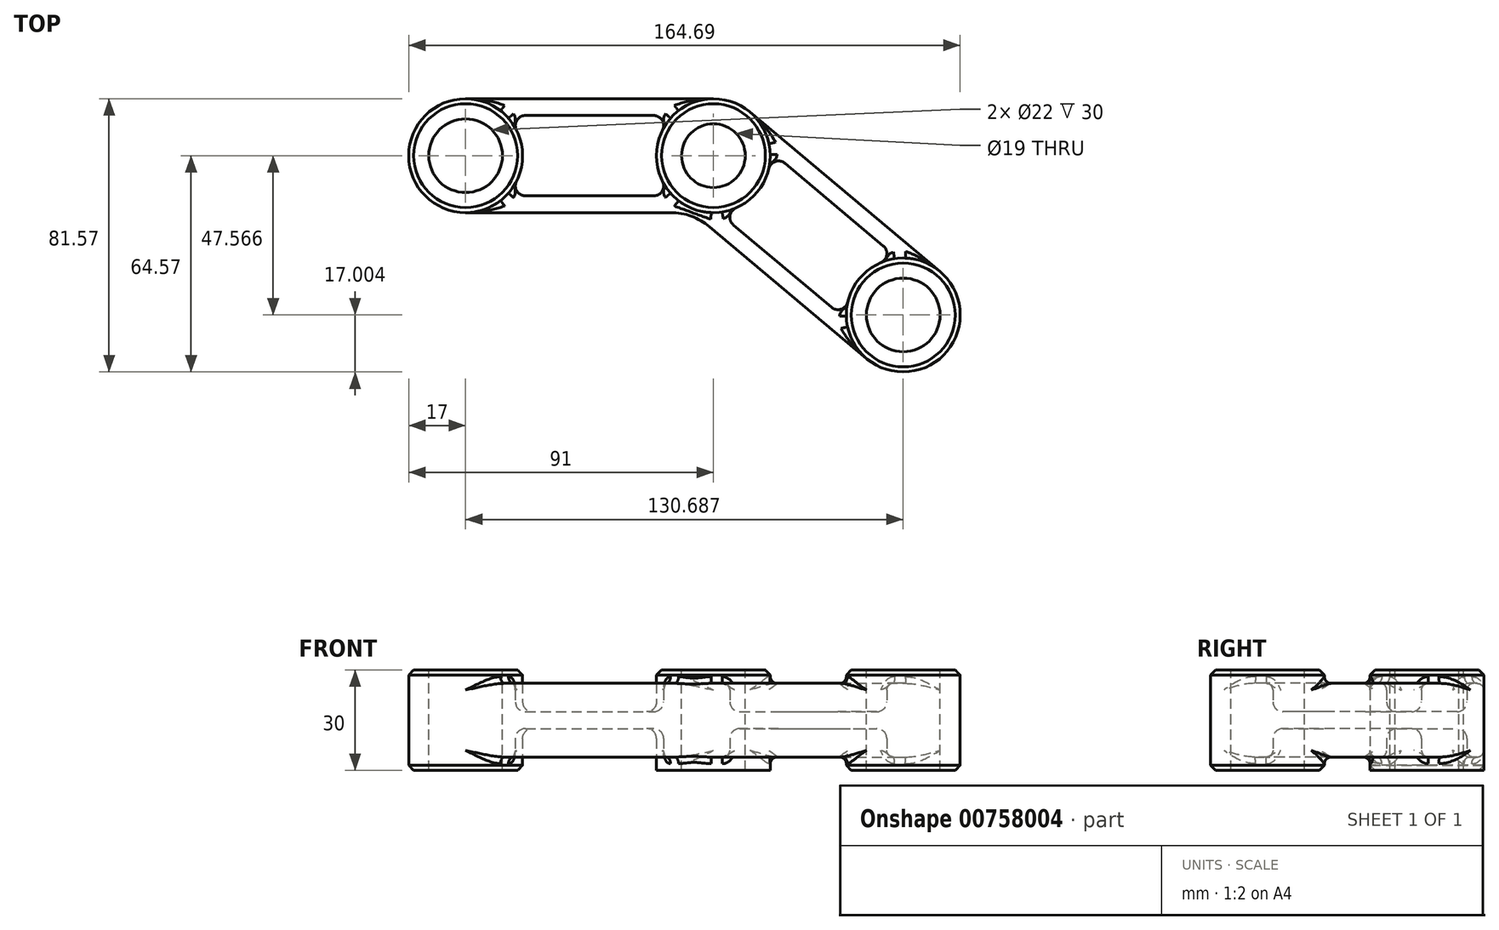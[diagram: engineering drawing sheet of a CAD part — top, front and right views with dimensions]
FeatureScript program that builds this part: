
annotation { "Feature Type Name" : "Feature", "Feature Type Description" : "" }
export const myFeature = defineFeature(function(context is Context, id is Id, definition is map)
    precondition{}
    {
        {
            var Q0;
            Q0=qCreatedBy(makeId("Top.planeOp"),FACE);
            var sketch = newSketch(context, id + "F0", { "sketchPlane" : qUnion([Q0])});
            skLineSegment(sketch, "E0", {"start": v(0, 0) * mm, "end": v(74, 0) * mm, "construction": true});
            skLineSegment(sketch, "E1", {"start": v(74, 0) * mm, "end": v(130.69, -47.57) * mm, "construction": true});
            skCircle(sketch, "E2", {"center": v(0, 0) * mm, "radius": 17 * mm});
            skCircle(sketch, "E3", {"center": v(74, 0) * mm, "radius": 17 * mm});
            skCircle(sketch, "E4", {"center": v(130.69, -47.57) * mm, "radius": 17 * mm});
            skCircle(sketch, "E5", {"center": v(0, 0) * mm, "radius": 11 * mm});
            skCircle(sketch, "E6", {"center": v(130.69, -47.57) * mm, "radius": 11 * mm});
            skCircle(sketch, "E7", {"center": v(74, 0) * mm, "radius": 9.5 * mm});
            skLineSegment(sketch, "E8", {"start": v(0, 0) * mm, "end": v(74, 0) * mm});
            skLineSegment(sketch, "E9", {"start": v(74, 0) * mm, "end": v(130.69, -47.57) * mm});
            skSolve(sketch);
        }
        {
            var Q0;
            Q0=qCreatedBy(makeId("Right.planeOp"),FACE);
            var sketch = newSketch(context, id + "F1", { "sketchPlane" : qUnion([Q0])});
            skLineSegment(sketch, "E10", {"start": v(-22.72, 0) * mm, "end": v(23.89, 0) * mm, "construction": true});
            skLineSegment(sketch, "E11", {"start": v(17, 0) * mm, "end": v(17, -11) * mm});
            skLineSegment(sketch, "E12", {"start": v(17, -11) * mm, "end": v(12, -11) * mm});
            skLineSegment(sketch, "E13", {"start": v(12, -11) * mm, "end": v(12, -2.5) * mm});
            skLineSegment(sketch, "E14", {"start": v(12, -2.5) * mm, "end": v(-12, -2.5) * mm});
            skLineSegment(sketch, "E15", {"start": v(-12, -2.5) * mm, "end": v(-12, -11) * mm});
            skLineSegment(sketch, "E16", {"start": v(-12, -11) * mm, "end": v(-17, -11) * mm});
            skLineSegment(sketch, "E17", {"start": v(-17, -11) * mm, "end": v(-17, 0) * mm});
            skLineSegment(sketch, "E18.MirrorCS", {"start": v(12, 2.5) * mm, "end": v(-12, 2.5) * mm});
            skLineSegment(sketch, "E19.MirrorCS", {"start": v(12, 11) * mm, "end": v(12, 2.5) * mm});
            skLineSegment(sketch, "E20.MirrorCS", {"start": v(-12, 2.5) * mm, "end": v(-12, 11) * mm});
            skLineSegment(sketch, "E21.MirrorCS", {"start": v(17, 0) * mm, "end": v(17, 11) * mm});
            skLineSegment(sketch, "E22.MirrorCS", {"start": v(-17, 11) * mm, "end": v(-17, 0) * mm});
            skLineSegment(sketch, "E23.MirrorCS", {"start": v(-12, 11) * mm, "end": v(-17, 11) * mm});
            skLineSegment(sketch, "E24.MirrorCS", {"start": v(17, 11) * mm, "end": v(12, 11) * mm});
            skLineSegment(sketch, "E25", {"start": v(0, 0) * mm, "end": v(0, 16.88) * mm, "construction": true});
            skSolve(sketch);
        }
        {
            var Q0;
            Q0=makeQuery(id+"F1.imprint","IMPRINT",FACE,{"disambiguationData":[TD([[makeQuery(id+"F1.imprint","IMPRINT",EDGE,{"derivedFrom":sQuery(id+"F1.wireOp",EDGE,"E11")}),-1.0]])]});
            var Q1;
            Q1=sQuery(id+"F0.wireOp",EDGE,"E8");
            var Q2;
            Q2=sQuery(id+"F0.wireOp",EDGE,"E9");
            sweep(context, id + "F2", {"profiles" : qUnion([Q0]), "path" : qUnion([Q1, Q2])});
        }
        {
            var Q0;
            Q0=makeQuery(id+"F0.imprint","IMPRINT",FACE,{"disambiguationData":[TD([[makeQuery(id+"F0.imprint","IMPRINT",EDGE,{"derivedFrom":sQuery(id+"F0.wireOp",EDGE,"E5")}),1.0]])]});
            var Q1;
            Q1=makeQuery(id+"F0.imprint","IMPRINT",FACE,{"disambiguationData":[TD([[makeQuery(id+"F0.imprint","IMPRINT",EDGE,{"derivedFrom":sQuery(id+"F0.wireOp",EDGE,"E2")}),1.0]])]});
            var Q2;
            {var subQ0=sQuery(id+"F0.wireOp",EDGE,"E8");var subQ1=sQuery(id+"F0.wireOp",EDGE,"E7");var subQ2=makeQuery(id+"F0.imprint","INTERSECT",VERTEX,{"derivedFrom":[subQ1,subQ0]});Q2=makeQuery(id+"F0.imprint","IMPRINT",FACE,{"disambiguationData":[TD([[makeQuery(id+"F0.imprint","IMPRINT",EDGE,{"disambiguationData":[TD([[subQ2,-1.0]])],"derivedFrom":subQ1}),1.0]])]});}
            var Q3;
            {var subQ0=sQuery(id+"F0.wireOp",EDGE,"E8");var subQ1=sQuery(id+"F0.wireOp",EDGE,"E7");var subQ2=makeQuery(id+"F0.imprint","INTERSECT",VERTEX,{"derivedFrom":[subQ1,subQ0]});Q3=makeQuery(id+"F0.imprint","IMPRINT",FACE,{"disambiguationData":[TD([[makeQuery(id+"F0.imprint","IMPRINT",EDGE,{"disambiguationData":[TD([[subQ2,1.0]])],"derivedFrom":subQ1}),1.0]])]});}
            var Q4;
            {var subQ0=sQuery(id+"F0.wireOp",EDGE,"E8");var subQ1=sQuery(id+"F0.wireOp",EDGE,"E3");var subQ2=makeQuery(id+"F0.imprint","INTERSECT",VERTEX,{"derivedFrom":[subQ1,subQ0]});Q4=makeQuery(id+"F0.imprint","IMPRINT",FACE,{"disambiguationData":[TD([[makeQuery(id+"F0.imprint","IMPRINT",EDGE,{"disambiguationData":[TD([[subQ2,1.0]])],"derivedFrom":subQ1}),1.0]])]});}
            var Q5;
            {var subQ0=sQuery(id+"F0.wireOp",EDGE,"E8");var subQ1=sQuery(id+"F0.wireOp",EDGE,"E3");var subQ2=makeQuery(id+"F0.imprint","INTERSECT",VERTEX,{"derivedFrom":[subQ1,subQ0]});Q5=makeQuery(id+"F0.imprint","IMPRINT",FACE,{"disambiguationData":[TD([[makeQuery(id+"F0.imprint","IMPRINT",EDGE,{"disambiguationData":[TD([[subQ2,-1.0]])],"derivedFrom":subQ1}),1.0]])]});}
            var Q6;
            Q6=makeQuery(id+"F0.imprint","IMPRINT",FACE,{"disambiguationData":[TD([[makeQuery(id+"F0.imprint","IMPRINT",EDGE,{"derivedFrom":sQuery(id+"F0.wireOp",EDGE,"E4")}),1.0]])]});
            var Q7;
            Q7=makeQuery(id+"F0.imprint","IMPRINT",FACE,{"disambiguationData":[TD([[makeQuery(id+"F0.imprint","IMPRINT",EDGE,{"derivedFrom":sQuery(id+"F0.wireOp",EDGE,"E6")}),1.0]])]});
            extrude(context, id + "F3", {"entities" : qUnion([Q0, Q1, Q2, Q3, Q4, Q5, Q6, Q7]), "operationType" : NewBodyOperationType.ADD, "depth" : 30 * mm, "offsetDistance" : 25 * mm, "symmetric" : true});
        }
        {
            var Q0;
            Q0=makeQuery(id+"F0.imprint","IMPRINT",FACE,{"disambiguationData":[TD([[makeQuery(id+"F0.imprint","IMPRINT",EDGE,{"derivedFrom":sQuery(id+"F0.wireOp",EDGE,"E5")}),1.0]])]});
            var Q1;
            {var subQ0=sQuery(id+"F0.wireOp",EDGE,"E8");var subQ1=sQuery(id+"F0.wireOp",EDGE,"E7");var subQ2=makeQuery(id+"F0.imprint","INTERSECT",VERTEX,{"derivedFrom":[subQ1,subQ0]});Q1=makeQuery(id+"F0.imprint","IMPRINT",FACE,{"disambiguationData":[TD([[makeQuery(id+"F0.imprint","IMPRINT",EDGE,{"disambiguationData":[TD([[subQ2,1.0]])],"derivedFrom":subQ1}),1.0]])]});}
            var Q2;
            {var subQ0=sQuery(id+"F0.wireOp",EDGE,"E8");var subQ1=sQuery(id+"F0.wireOp",EDGE,"E7");var subQ2=makeQuery(id+"F0.imprint","INTERSECT",VERTEX,{"derivedFrom":[subQ1,subQ0]});Q2=makeQuery(id+"F0.imprint","IMPRINT",FACE,{"disambiguationData":[TD([[makeQuery(id+"F0.imprint","IMPRINT",EDGE,{"disambiguationData":[TD([[subQ2,-1.0]])],"derivedFrom":subQ1}),1.0]])]});}
            var Q3;
            Q3=makeQuery(id+"F0.imprint","IMPRINT",FACE,{"disambiguationData":[TD([[makeQuery(id+"F0.imprint","IMPRINT",EDGE,{"derivedFrom":sQuery(id+"F0.wireOp",EDGE,"E6")}),1.0]])]});
            extrude(context, id + "F4", {"entities" : qUnion([Q0, Q1, Q2, Q3]), "operationType" : NewBodyOperationType.REMOVE, "oppositeDirection" : true, "depth" : 30 * mm, "offsetDistance" : 25 * mm, "symmetric" : true});
        }
        {
            var Q0;
            {var subQ0=sQuery(id+"F1.wireOp",EDGE,"E21.MirrorCS");var subQ1=sQuery(id+"F1.wireOp",EDGE,"E11");var subQ2=sQuery(id+"F0.wireOp",EDGE,"E8");var subQ3=makeQuery(id+"F2.opSweep","SWEPT_FACE",FACE,{"disambiguationData":[OSD([subQ2,sQuery(id+"F1.wireOp",EDGE,"E24.MirrorCS")])]});Q0=makeQuery(id+"F3.boolean.opBoolean","SPLIT",FACE,{"disambiguationData":[TD([makeQuery(id+"F2.opSweep","SWEPT_FACE",FACE,{"disambiguationData":[OSD([subQ2,subQ1,subQ0])]}),subQ3,makeQuery(id+"F2.opSweep","SWEPT_FACE",FACE,{"disambiguationData":[OSD([sQuery(id+"F0.wireOp",EDGE,"E9"),subQ1,subQ0])]}),makeQuery(id+"F3.opExtrude","SWEPT_FACE",FACE,{"disambiguationData":[OSD([sQuery(id+"F0.wireOp",EDGE,"E3")])]})])],"derivedFrom":subQ3});}
            var sketch = newSketch(context, id + "F5", { "sketchPlane" : qUnion([Q0])});
            skLineSegment(sketch, "E26.0.0", {"start": v(80.19, 17) * mm, "end": v(74, 17) * mm});
            skArc(sketch, "E26.0.1", {"start": v(74, 17) * mm, "mid": v(79.81, 15.97) * mm, "end": v(84.93, 13.02) * mm});
            skLineSegment(sketch, "E26.0.2", {"start": v(84.93, 13.02) * mm, "end": v(80.19, 17) * mm});
            skSolve(sketch);
        }
        {
            var Q0;
            Q0=qSketchRegion(id+"F5",true);
            extrude(context, id + "F6", {"entities" : qUnion([Q0]), "operationType" : NewBodyOperationType.REMOVE, "endBound" : BoundingType.THROUGH_ALL, "oppositeDirection" : true, "depth" : 25 * mm, "offsetDistance" : 25 * mm});
        }
        {
            var Q0;
            Q0=makeQuery(id+"F2.opSweep","MID_CAP_EDGE",EDGE,{"disambiguationData":[OSD([sQuery(id+"F0.wireOp",VERTEX,"E9.start"),sQuery(id+"F1.wireOp",EDGE,"E17"),sQuery(id+"F1.wireOp",EDGE,"E22.MirrorCS")])],"capPos":1.0});
            fillet(context, id + "F7", {"entities" : qUnion([Q0]), "radius" : 18 * mm, "tangentPropagation" : true, "allowEdgeOverflow" : false});
        }
        {
            var Q0;
            Q0=makeQuery(id+"F3.opExtrude","CAP_EDGE",EDGE,{"disambiguationData":[OSD([sQuery(id+"F0.wireOp",EDGE,"E2")])],"isStart":false});
            var Q1;
            Q1=makeQuery(id+"F3.opExtrude","CAP_EDGE",EDGE,{"disambiguationData":[OSD([sQuery(id+"F0.wireOp",EDGE,"E2")])],"isStart":true});
            var Q2;
            Q2=makeQuery(id+"F3.opExtrude","CAP_EDGE",EDGE,{"disambiguationData":[OSD([sQuery(id+"F0.wireOp",EDGE,"E3")])],"isStart":true});
            var Q3;
            Q3=makeQuery(id+"F3.opExtrude","CAP_EDGE",EDGE,{"disambiguationData":[OSD([sQuery(id+"F0.wireOp",EDGE,"E3")])],"isStart":false});
            var Q4;
            Q4=makeQuery(id+"F3.opExtrude","CAP_EDGE",EDGE,{"disambiguationData":[OSD([sQuery(id+"F0.wireOp",EDGE,"E4")])],"isStart":false});
            var Q5;
            Q5=makeQuery(id+"F3.opExtrude","CAP_EDGE",EDGE,{"disambiguationData":[OSD([sQuery(id+"F0.wireOp",EDGE,"E4")])],"isStart":true});
            chamfer(context, id + "F8", {"entities" : qUnion([Q0, Q1, Q2, Q3, Q4, Q5]), "width" : 1.5 * mm, "tangentPropagation" : true});
        }
        {
            var Q0;
            Q0=makeQuery(id+"F2.opSweep","SWEPT_EDGE",EDGE,{"disambiguationData":[OSD([sQuery(id+"F0.wireOp",EDGE,"E8"),sQuery(id+"F1.wireOp",EDGE,"E22.MirrorCS"),sQuery(id+"F1.wireOp",EDGE,"E23.MirrorCS")])]});
            var Q1;
            Q1=makeQuery(id+"F2.opSweep","SWEPT_EDGE",EDGE,{"disambiguationData":[OSD([sQuery(id+"F0.wireOp",EDGE,"E8"),sQuery(id+"F1.wireOp",EDGE,"E16"),sQuery(id+"F1.wireOp",EDGE,"E17")])]});
            var Q2;
            {var subQ0=sQuery(id+"F1.wireOp",EDGE,"E21.MirrorCS");var subQ1=sQuery(id+"F0.wireOp",EDGE,"E8");var subQ2=sQuery(id+"F1.wireOp",EDGE,"E24.MirrorCS");Q2=makeQuery(id+"F3.boolean.opBoolean","SPLIT",EDGE,{"disambiguationData":[TD([makeQuery(id+"F3.opExtrude","SWEPT_FACE",FACE,{"disambiguationData":[OSD([sQuery(id+"F0.wireOp",EDGE,"E2")])]})])],"derivedFrom":makeQuery(id+"F2.opSweep","SWEPT_EDGE",EDGE,{"disambiguationData":[OSD([subQ1,subQ0,subQ2])]})});}
            var Q3;
            {var subQ0=sQuery(id+"F1.wireOp",EDGE,"E24.MirrorCS");var subQ1=sQuery(id+"F1.wireOp",EDGE,"E21.MirrorCS");var subQ2=sQuery(id+"F0.wireOp",EDGE,"E9");Q3=makeQuery(id+"F3.boolean.opBoolean","SPLIT",EDGE,{"disambiguationData":[TD([makeQuery(id+"F3.opExtrude","SWEPT_FACE",FACE,{"disambiguationData":[OSD([sQuery(id+"F0.wireOp",EDGE,"E4")])]})])],"derivedFrom":makeQuery(id+"F2.opSweep","SWEPT_EDGE",EDGE,{"disambiguationData":[OSD([subQ2,subQ1,subQ0])]})});}
            var Q4;
            {var subQ0=sQuery(id+"F1.wireOp",EDGE,"E11");var subQ1=sQuery(id+"F0.wireOp",EDGE,"E8");var subQ2=sQuery(id+"F1.wireOp",EDGE,"E12");Q4=makeQuery(id+"F3.boolean.opBoolean","SPLIT",EDGE,{"disambiguationData":[TD([makeQuery(id+"F3.opExtrude","SWEPT_FACE",FACE,{"disambiguationData":[OSD([sQuery(id+"F0.wireOp",EDGE,"E2")])]})])],"derivedFrom":makeQuery(id+"F2.opSweep","SWEPT_EDGE",EDGE,{"disambiguationData":[OSD([subQ1,subQ0,subQ2])]})});}
            var Q5;
            {var subQ0=sQuery(id+"F1.wireOp",EDGE,"E12");var subQ1=sQuery(id+"F1.wireOp",EDGE,"E11");var subQ2=sQuery(id+"F0.wireOp",EDGE,"E9");Q5=makeQuery(id+"F3.boolean.opBoolean","SPLIT",EDGE,{"disambiguationData":[TD([makeQuery(id+"F3.opExtrude","SWEPT_FACE",FACE,{"disambiguationData":[OSD([sQuery(id+"F0.wireOp",EDGE,"E4")])]})])],"derivedFrom":makeQuery(id+"F2.opSweep","SWEPT_EDGE",EDGE,{"disambiguationData":[OSD([subQ2,subQ1,subQ0])]})});}
            fillet(context, id + "F9", {"entities" : qUnion([Q0, Q1, Q2, Q3, Q4, Q5]), "radius" : 2 * mm, "tangentPropagation" : true, "allowEdgeOverflow" : false});
        }
        {
            var Q0;
            {var subQ0=sQuery(id+"F0.wireOp",EDGE,"E8");Q0=makeQuery(id+"F3.boolean.opBoolean","SPLIT",FACE,{"disambiguationData":[TD([makeQuery(id+"F3.opExtrude","SWEPT_FACE",FACE,{"disambiguationData":[OSD([sQuery(id+"F0.wireOp",EDGE,"E2")])]})])],"derivedFrom":makeQuery(id+"F2.opSweep","SWEPT_FACE",FACE,{"disambiguationData":[OSD([subQ0,sQuery(id+"F1.wireOp",EDGE,"E18.MirrorCS")])]})});}
            var Q1;
            Q1=makeQuery(id+"F3.boolean.opBoolean","INTERSECT",EDGE,{"derivedFrom":[makeQuery(id+"F2.opSweep","SWEPT_FACE",FACE,{"disambiguationData":[OSD([sQuery(id+"F0.wireOp",EDGE,"E8"),sQuery(id+"F1.wireOp",EDGE,"E19.MirrorCS")])]}),makeQuery(id+"F3.opExtrude","SWEPT_FACE",FACE,{"disambiguationData":[OSD([sQuery(id+"F0.wireOp",EDGE,"E3")])]})]});
            var Q2;
            Q2=makeQuery(id+"F3.boolean.opBoolean","INTERSECT",EDGE,{"derivedFrom":[makeQuery(id+"F2.opSweep","SWEPT_FACE",FACE,{"disambiguationData":[OSD([sQuery(id+"F0.wireOp",EDGE,"E8"),sQuery(id+"F1.wireOp",EDGE,"E19.MirrorCS")])]}),makeQuery(id+"F3.opExtrude","SWEPT_FACE",FACE,{"disambiguationData":[OSD([sQuery(id+"F0.wireOp",EDGE,"E2")])]})]});
            var Q3;
            Q3=makeQuery(id+"F3.boolean.opBoolean","INTERSECT",EDGE,{"derivedFrom":[makeQuery(id+"F2.opSweep","SWEPT_FACE",FACE,{"disambiguationData":[OSD([sQuery(id+"F0.wireOp",EDGE,"E8"),sQuery(id+"F1.wireOp",EDGE,"E20.MirrorCS")])]}),makeQuery(id+"F3.opExtrude","SWEPT_FACE",FACE,{"disambiguationData":[OSD([sQuery(id+"F0.wireOp",EDGE,"E2")])]})]});
            var Q4;
            Q4=makeQuery(id+"F3.boolean.opBoolean","INTERSECT",EDGE,{"derivedFrom":[makeQuery(id+"F2.opSweep","SWEPT_FACE",FACE,{"disambiguationData":[OSD([sQuery(id+"F0.wireOp",EDGE,"E8"),sQuery(id+"F1.wireOp",EDGE,"E20.MirrorCS")])]}),makeQuery(id+"F3.opExtrude","SWEPT_FACE",FACE,{"disambiguationData":[OSD([sQuery(id+"F0.wireOp",EDGE,"E3")])]})]});
            var Q5;
            Q5=makeQuery(id+"F3.boolean.opBoolean","SPLIT",FACE,{"disambiguationData":[TD([makeQuery(id+"F3.opExtrude","SWEPT_FACE",FACE,{"disambiguationData":[OSD([sQuery(id+"F0.wireOp",EDGE,"E4")])]})])],"derivedFrom":makeQuery(id+"F2.opSweep","SWEPT_FACE",FACE,{"disambiguationData":[OSD([sQuery(id+"F0.wireOp",EDGE,"E8"),sQuery(id+"F1.wireOp",EDGE,"E18.MirrorCS")])]})});
            var Q6;
            Q6=makeQuery(id+"F3.boolean.opBoolean","INTERSECT",EDGE,{"derivedFrom":[makeQuery(id+"F2.opSweep","SWEPT_FACE",FACE,{"disambiguationData":[OSD([sQuery(id+"F0.wireOp",EDGE,"E9"),sQuery(id+"F1.wireOp",EDGE,"E19.MirrorCS")])]}),makeQuery(id+"F3.opExtrude","SWEPT_FACE",FACE,{"disambiguationData":[OSD([sQuery(id+"F0.wireOp",EDGE,"E3")])]})]});
            var Q7;
            Q7=makeQuery(id+"F3.boolean.opBoolean","INTERSECT",EDGE,{"derivedFrom":[makeQuery(id+"F2.opSweep","SWEPT_FACE",FACE,{"disambiguationData":[OSD([sQuery(id+"F0.wireOp",EDGE,"E9"),sQuery(id+"F1.wireOp",EDGE,"E20.MirrorCS")])]}),makeQuery(id+"F3.opExtrude","SWEPT_FACE",FACE,{"disambiguationData":[OSD([sQuery(id+"F0.wireOp",EDGE,"E3")])]})]});
            var Q8;
            Q8=makeQuery(id+"F3.boolean.opBoolean","INTERSECT",EDGE,{"derivedFrom":[makeQuery(id+"F2.opSweep","SWEPT_FACE",FACE,{"disambiguationData":[OSD([sQuery(id+"F0.wireOp",EDGE,"E9"),sQuery(id+"F1.wireOp",EDGE,"E20.MirrorCS")])]}),makeQuery(id+"F3.opExtrude","SWEPT_FACE",FACE,{"disambiguationData":[OSD([sQuery(id+"F0.wireOp",EDGE,"E4")])]})]});
            var Q9;
            Q9=makeQuery(id+"F3.boolean.opBoolean","INTERSECT",EDGE,{"derivedFrom":[makeQuery(id+"F2.opSweep","SWEPT_FACE",FACE,{"disambiguationData":[OSD([sQuery(id+"F0.wireOp",EDGE,"E9"),sQuery(id+"F1.wireOp",EDGE,"E19.MirrorCS")])]}),makeQuery(id+"F3.opExtrude","SWEPT_FACE",FACE,{"disambiguationData":[OSD([sQuery(id+"F0.wireOp",EDGE,"E4")])]})]});
            var Q10;
            {var subQ0=sQuery(id+"F0.wireOp",EDGE,"E8");Q10=makeQuery(id+"F3.boolean.opBoolean","SPLIT",FACE,{"disambiguationData":[TD([makeQuery(id+"F3.opExtrude","SWEPT_FACE",FACE,{"disambiguationData":[OSD([sQuery(id+"F0.wireOp",EDGE,"E2")])]})])],"derivedFrom":makeQuery(id+"F2.opSweep","SWEPT_FACE",FACE,{"disambiguationData":[OSD([subQ0,sQuery(id+"F1.wireOp",EDGE,"E14")])]})});}
            var Q11;
            Q11=makeQuery(id+"F3.boolean.opBoolean","SPLIT",FACE,{"disambiguationData":[TD([makeQuery(id+"F3.opExtrude","SWEPT_FACE",FACE,{"disambiguationData":[OSD([sQuery(id+"F0.wireOp",EDGE,"E4")])]})])],"derivedFrom":makeQuery(id+"F2.opSweep","SWEPT_FACE",FACE,{"disambiguationData":[OSD([sQuery(id+"F0.wireOp",EDGE,"E8"),sQuery(id+"F1.wireOp",EDGE,"E14")])]})});
            var Q12;
            Q12=makeQuery(id+"F3.boolean.opBoolean","INTERSECT",EDGE,{"derivedFrom":[makeQuery(id+"F2.opSweep","SWEPT_FACE",FACE,{"disambiguationData":[OSD([sQuery(id+"F0.wireOp",EDGE,"E8"),sQuery(id+"F1.wireOp",EDGE,"E15")])]}),makeQuery(id+"F3.opExtrude","SWEPT_FACE",FACE,{"disambiguationData":[OSD([sQuery(id+"F0.wireOp",EDGE,"E2")])]})]});
            var Q13;
            Q13=makeQuery(id+"F3.boolean.opBoolean","INTERSECT",EDGE,{"derivedFrom":[makeQuery(id+"F2.opSweep","SWEPT_FACE",FACE,{"disambiguationData":[OSD([sQuery(id+"F0.wireOp",EDGE,"E8"),sQuery(id+"F1.wireOp",EDGE,"E13")])]}),makeQuery(id+"F3.opExtrude","SWEPT_FACE",FACE,{"disambiguationData":[OSD([sQuery(id+"F0.wireOp",EDGE,"E2")])]})]});
            var Q14;
            Q14=makeQuery(id+"F3.boolean.opBoolean","INTERSECT",EDGE,{"derivedFrom":[makeQuery(id+"F2.opSweep","SWEPT_FACE",FACE,{"disambiguationData":[OSD([sQuery(id+"F0.wireOp",EDGE,"E8"),sQuery(id+"F1.wireOp",EDGE,"E15")])]}),makeQuery(id+"F3.opExtrude","SWEPT_FACE",FACE,{"disambiguationData":[OSD([sQuery(id+"F0.wireOp",EDGE,"E3")])]})]});
            var Q15;
            Q15=makeQuery(id+"F3.boolean.opBoolean","INTERSECT",EDGE,{"derivedFrom":[makeQuery(id+"F2.opSweep","SWEPT_FACE",FACE,{"disambiguationData":[OSD([sQuery(id+"F0.wireOp",EDGE,"E8"),sQuery(id+"F1.wireOp",EDGE,"E13")])]}),makeQuery(id+"F3.opExtrude","SWEPT_FACE",FACE,{"disambiguationData":[OSD([sQuery(id+"F0.wireOp",EDGE,"E3")])]})]});
            var Q16;
            Q16=makeQuery(id+"F3.boolean.opBoolean","INTERSECT",EDGE,{"derivedFrom":[makeQuery(id+"F2.opSweep","SWEPT_FACE",FACE,{"disambiguationData":[OSD([sQuery(id+"F0.wireOp",EDGE,"E9"),sQuery(id+"F1.wireOp",EDGE,"E15")])]}),makeQuery(id+"F3.opExtrude","SWEPT_FACE",FACE,{"disambiguationData":[OSD([sQuery(id+"F0.wireOp",EDGE,"E4")])]})]});
            var Q17;
            Q17=makeQuery(id+"F3.boolean.opBoolean","INTERSECT",EDGE,{"derivedFrom":[makeQuery(id+"F2.opSweep","SWEPT_FACE",FACE,{"disambiguationData":[OSD([sQuery(id+"F0.wireOp",EDGE,"E9"),sQuery(id+"F1.wireOp",EDGE,"E13")])]}),makeQuery(id+"F3.opExtrude","SWEPT_FACE",FACE,{"disambiguationData":[OSD([sQuery(id+"F0.wireOp",EDGE,"E4")])]})]});
            var Q18;
            Q18=makeQuery(id+"F3.boolean.opBoolean","INTERSECT",EDGE,{"derivedFrom":[makeQuery(id+"F2.opSweep","SWEPT_FACE",FACE,{"disambiguationData":[OSD([sQuery(id+"F0.wireOp",EDGE,"E9"),sQuery(id+"F1.wireOp",EDGE,"E15")])]}),makeQuery(id+"F3.opExtrude","SWEPT_FACE",FACE,{"disambiguationData":[OSD([sQuery(id+"F0.wireOp",EDGE,"E3")])]})]});
            var Q19;
            Q19=makeQuery(id+"F3.boolean.opBoolean","INTERSECT",EDGE,{"derivedFrom":[makeQuery(id+"F2.opSweep","SWEPT_FACE",FACE,{"disambiguationData":[OSD([sQuery(id+"F0.wireOp",EDGE,"E9"),sQuery(id+"F1.wireOp",EDGE,"E13")])]}),makeQuery(id+"F3.opExtrude","SWEPT_FACE",FACE,{"disambiguationData":[OSD([sQuery(id+"F0.wireOp",EDGE,"E3")])]})]});
            fillet(context, id + "F10", {"entities" : qUnion([Q0, Q1, Q2, Q3, Q4, Q5, Q6, Q7, Q8, Q9, Q10, Q11, Q12, Q13, Q14, Q15, Q16, Q17, Q18, Q19]), "radius" : 3 * mm, "tangentPropagation" : true, "allowEdgeOverflow" : false});
        }
        {
            var Q0;
            Q0=makeQuery(id+"F2.opSweep","SWEPT_EDGE",EDGE,{"disambiguationData":[OSD([sQuery(id+"F0.wireOp",EDGE,"E8"),sQuery(id+"F1.wireOp",EDGE,"E19.MirrorCS"),sQuery(id+"F1.wireOp",EDGE,"E24.MirrorCS")])]});
            var Q1;
            Q1=makeQuery(id+"F2.opSweep","SWEPT_EDGE",EDGE,{"disambiguationData":[OSD([sQuery(id+"F0.wireOp",EDGE,"E8"),sQuery(id+"F1.wireOp",EDGE,"E20.MirrorCS"),sQuery(id+"F1.wireOp",EDGE,"E23.MirrorCS")])]});
            var Q2;
            Q2=makeQuery(id+"F2.opSweep","SWEPT_EDGE",EDGE,{"disambiguationData":[OSD([sQuery(id+"F0.wireOp",EDGE,"E9"),sQuery(id+"F1.wireOp",EDGE,"E19.MirrorCS"),sQuery(id+"F1.wireOp",EDGE,"E24.MirrorCS")])]});
            var Q3;
            Q3=makeQuery(id+"F2.opSweep","SWEPT_EDGE",EDGE,{"disambiguationData":[OSD([sQuery(id+"F0.wireOp",EDGE,"E9"),sQuery(id+"F1.wireOp",EDGE,"E20.MirrorCS"),sQuery(id+"F1.wireOp",EDGE,"E23.MirrorCS")])]});
            var Q4;
            Q4=makeQuery(id+"F2.opSweep","SWEPT_EDGE",EDGE,{"disambiguationData":[OSD([sQuery(id+"F0.wireOp",EDGE,"E8"),sQuery(id+"F1.wireOp",EDGE,"E15"),sQuery(id+"F1.wireOp",EDGE,"E16")])]});
            var Q5;
            Q5=makeQuery(id+"F2.opSweep","SWEPT_EDGE",EDGE,{"disambiguationData":[OSD([sQuery(id+"F0.wireOp",EDGE,"E8"),sQuery(id+"F1.wireOp",EDGE,"E12"),sQuery(id+"F1.wireOp",EDGE,"E13")])]});
            var Q6;
            Q6=makeQuery(id+"F2.opSweep","SWEPT_EDGE",EDGE,{"disambiguationData":[OSD([sQuery(id+"F0.wireOp",EDGE,"E9"),sQuery(id+"F1.wireOp",EDGE,"E12"),sQuery(id+"F1.wireOp",EDGE,"E13")])]});
            var Q7;
            Q7=makeQuery(id+"F2.opSweep","SWEPT_EDGE",EDGE,{"disambiguationData":[OSD([sQuery(id+"F0.wireOp",EDGE,"E9"),sQuery(id+"F1.wireOp",EDGE,"E15"),sQuery(id+"F1.wireOp",EDGE,"E16")])]});
            fillet(context, id + "F11", {"entities" : qUnion([Q0, Q1, Q2, Q3, Q4, Q5, Q6, Q7]), "radius" : 2 * mm, "tangentPropagation" : true, "allowEdgeOverflow" : false});
        }
        {
            var Q0;
            Q0=makeQuery(id+"F3.boolean.opBoolean","INTERSECT",EDGE,{"derivedFrom":[makeQuery(id+"F2.opSweep","SWEPT_FACE",FACE,{"disambiguationData":[OSD([sQuery(id+"F0.wireOp",EDGE,"E8"),sQuery(id+"F1.wireOp",EDGE,"E23.MirrorCS")])]}),makeQuery(id+"F3.opExtrude","SWEPT_FACE",FACE,{"disambiguationData":[OSD([sQuery(id+"F0.wireOp",EDGE,"E3")])]})]});
            var Q1;
            Q1=makeQuery(id+"F3.boolean.opBoolean","INTERSECT",EDGE,{"derivedFrom":[makeQuery(id+"F2.opSweep","SWEPT_FACE",FACE,{"disambiguationData":[OSD([sQuery(id+"F0.wireOp",EDGE,"E8"),sQuery(id+"F1.wireOp",EDGE,"E23.MirrorCS")])]}),makeQuery(id+"F3.opExtrude","SWEPT_FACE",FACE,{"disambiguationData":[OSD([sQuery(id+"F0.wireOp",EDGE,"E2")])]})]});
            var Q2;
            Q2=makeQuery(id+"F3.boolean.opBoolean","INTERSECT",EDGE,{"derivedFrom":[makeQuery(id+"F2.opSweep","SWEPT_FACE",FACE,{"disambiguationData":[OSD([sQuery(id+"F0.wireOp",EDGE,"E8"),sQuery(id+"F1.wireOp",EDGE,"E24.MirrorCS")])]}),makeQuery(id+"F3.opExtrude","SWEPT_FACE",FACE,{"disambiguationData":[OSD([sQuery(id+"F0.wireOp",EDGE,"E2")])]})]});
            var Q3;
            Q3=makeQuery(id+"F3.boolean.opBoolean","INTERSECT",EDGE,{"disambiguationData":[OD(1.0)],"derivedFrom":[makeQuery(id+"F2.opSweep","SWEPT_FACE",FACE,{"disambiguationData":[OSD([sQuery(id+"F0.wireOp",EDGE,"E8"),sQuery(id+"F1.wireOp",EDGE,"E24.MirrorCS")])]}),makeQuery(id+"F3.opExtrude","SWEPT_FACE",FACE,{"disambiguationData":[OSD([sQuery(id+"F0.wireOp",EDGE,"E3")])]})]});
            var Q4;
            Q4=makeQuery(id+"F3.boolean.opBoolean","INTERSECT",EDGE,{"disambiguationData":[OD(0.0)],"derivedFrom":[makeQuery(id+"F2.opSweep","SWEPT_FACE",FACE,{"disambiguationData":[OSD([sQuery(id+"F0.wireOp",EDGE,"E8"),sQuery(id+"F1.wireOp",EDGE,"E24.MirrorCS")])]}),makeQuery(id+"F3.opExtrude","SWEPT_FACE",FACE,{"disambiguationData":[OSD([sQuery(id+"F0.wireOp",EDGE,"E3")])]})]});
            var Q5;
            Q5=makeQuery(id+"F3.boolean.opBoolean","INTERSECT",EDGE,{"derivedFrom":[makeQuery(id+"F2.opSweep","SWEPT_FACE",FACE,{"disambiguationData":[OSD([sQuery(id+"F0.wireOp",EDGE,"E8"),sQuery(id+"F1.wireOp",EDGE,"E23.MirrorCS")])]}),makeQuery(id+"F3.opExtrude","SWEPT_FACE",FACE,{"disambiguationData":[OSD([sQuery(id+"F0.wireOp",EDGE,"E4")])]})]});
            var Q6;
            Q6=makeQuery(id+"F3.boolean.opBoolean","INTERSECT",EDGE,{"derivedFrom":[makeQuery(id+"F2.opSweep","SWEPT_FACE",FACE,{"disambiguationData":[OSD([sQuery(id+"F0.wireOp",EDGE,"E8"),sQuery(id+"F1.wireOp",EDGE,"E24.MirrorCS")])]}),makeQuery(id+"F3.opExtrude","SWEPT_FACE",FACE,{"disambiguationData":[OSD([sQuery(id+"F0.wireOp",EDGE,"E4")])]})]});
            var Q7;
            Q7=makeQuery(id+"F3.boolean.opBoolean","INTERSECT",EDGE,{"derivedFrom":[makeQuery(id+"F2.opSweep","SWEPT_FACE",FACE,{"disambiguationData":[OSD([sQuery(id+"F0.wireOp",EDGE,"E8"),sQuery(id+"F1.wireOp",EDGE,"E16")])]}),makeQuery(id+"F3.opExtrude","SWEPT_FACE",FACE,{"disambiguationData":[OSD([sQuery(id+"F0.wireOp",EDGE,"E3")])]})]});
            var Q8;
            Q8=makeQuery(id+"F3.boolean.opBoolean","INTERSECT",EDGE,{"disambiguationData":[OD(0.0)],"derivedFrom":[makeQuery(id+"F2.opSweep","SWEPT_FACE",FACE,{"disambiguationData":[OSD([sQuery(id+"F0.wireOp",EDGE,"E8"),sQuery(id+"F1.wireOp",EDGE,"E12")])]}),makeQuery(id+"F3.opExtrude","SWEPT_FACE",FACE,{"disambiguationData":[OSD([sQuery(id+"F0.wireOp",EDGE,"E3")])]})]});
            var Q9;
            Q9=makeQuery(id+"F3.boolean.opBoolean","INTERSECT",EDGE,{"disambiguationData":[OD(1.0)],"derivedFrom":[makeQuery(id+"F2.opSweep","SWEPT_FACE",FACE,{"disambiguationData":[OSD([sQuery(id+"F0.wireOp",EDGE,"E8"),sQuery(id+"F1.wireOp",EDGE,"E12")])]}),makeQuery(id+"F3.opExtrude","SWEPT_FACE",FACE,{"disambiguationData":[OSD([sQuery(id+"F0.wireOp",EDGE,"E3")])]})]});
            var Q10;
            Q10=makeQuery(id+"F3.boolean.opBoolean","INTERSECT",EDGE,{"derivedFrom":[makeQuery(id+"F2.opSweep","SWEPT_FACE",FACE,{"disambiguationData":[OSD([sQuery(id+"F0.wireOp",EDGE,"E8"),sQuery(id+"F1.wireOp",EDGE,"E12")])]}),makeQuery(id+"F3.opExtrude","SWEPT_FACE",FACE,{"disambiguationData":[OSD([sQuery(id+"F0.wireOp",EDGE,"E2")])]})]});
            var Q11;
            Q11=makeQuery(id+"F3.boolean.opBoolean","INTERSECT",EDGE,{"derivedFrom":[makeQuery(id+"F2.opSweep","SWEPT_FACE",FACE,{"disambiguationData":[OSD([sQuery(id+"F0.wireOp",EDGE,"E8"),sQuery(id+"F1.wireOp",EDGE,"E16")])]}),makeQuery(id+"F3.opExtrude","SWEPT_FACE",FACE,{"disambiguationData":[OSD([sQuery(id+"F0.wireOp",EDGE,"E2")])]})]});
            var Q12;
            Q12=makeQuery(id+"F3.boolean.opBoolean","INTERSECT",EDGE,{"derivedFrom":[makeQuery(id+"F2.opSweep","SWEPT_FACE",FACE,{"disambiguationData":[OSD([sQuery(id+"F0.wireOp",EDGE,"E8"),sQuery(id+"F1.wireOp",EDGE,"E12")])]}),makeQuery(id+"F3.opExtrude","SWEPT_FACE",FACE,{"disambiguationData":[OSD([sQuery(id+"F0.wireOp",EDGE,"E4")])]})]});
            var Q13;
            Q13=makeQuery(id+"F3.boolean.opBoolean","INTERSECT",EDGE,{"derivedFrom":[makeQuery(id+"F2.opSweep","SWEPT_FACE",FACE,{"disambiguationData":[OSD([sQuery(id+"F0.wireOp",EDGE,"E8"),sQuery(id+"F1.wireOp",EDGE,"E16")])]}),makeQuery(id+"F3.opExtrude","SWEPT_FACE",FACE,{"disambiguationData":[OSD([sQuery(id+"F0.wireOp",EDGE,"E4")])]})]});
            fillet(context, id + "F12", {"entities" : qUnion([Q0, Q1, Q2, Q3, Q4, Q5, Q6, Q7, Q8, Q9, Q10, Q11, Q12, Q13]), "radius" : 2 * mm, "tangentPropagation" : true, "allowEdgeOverflow" : false});
        }
    });
